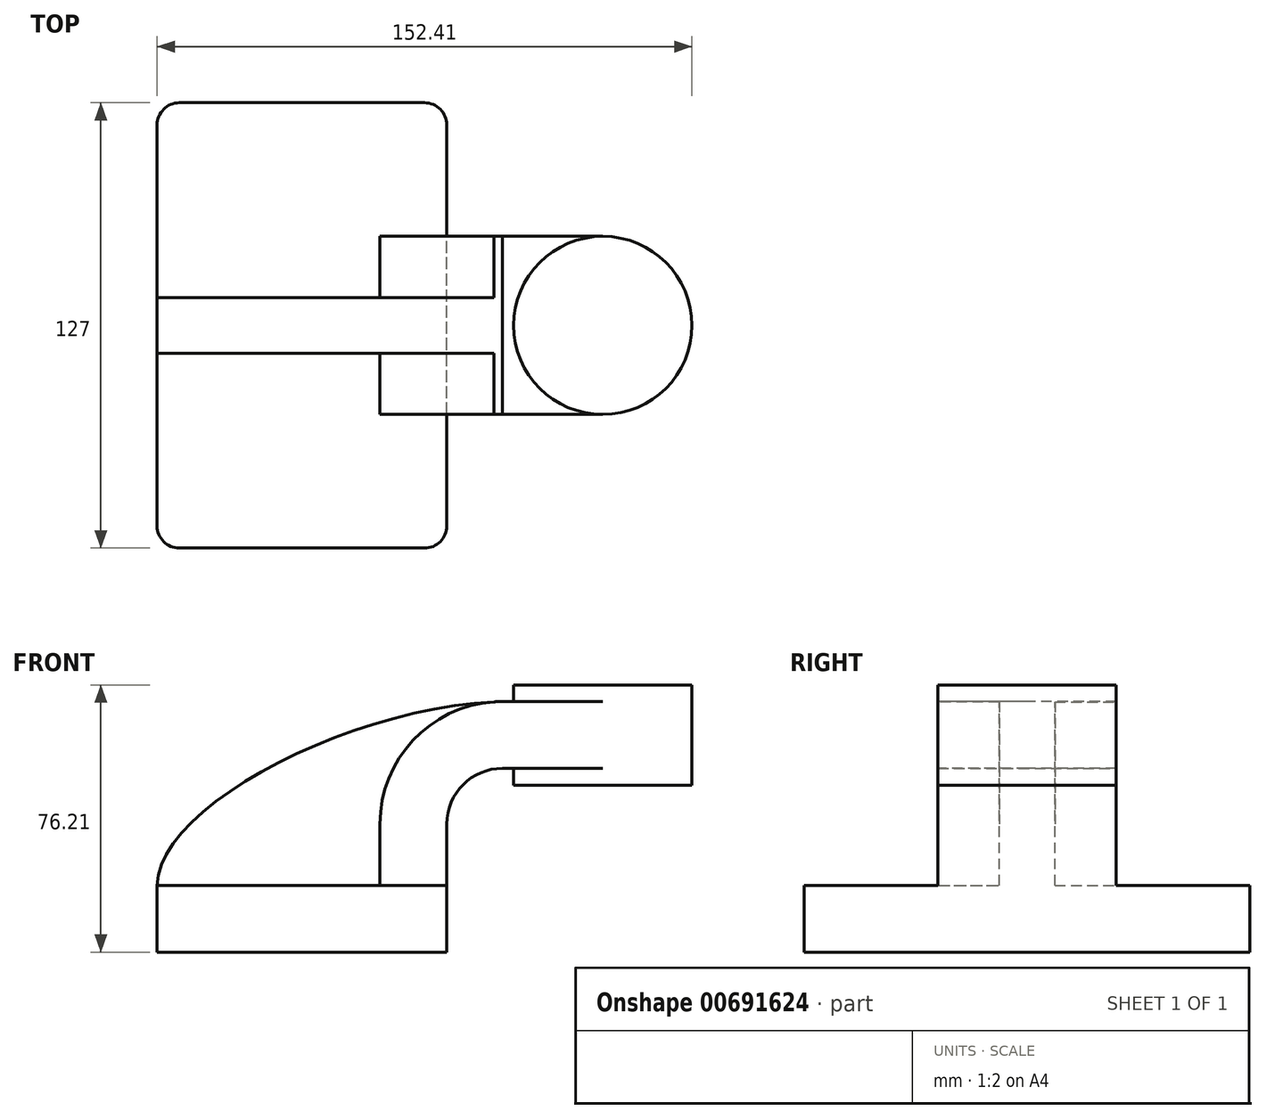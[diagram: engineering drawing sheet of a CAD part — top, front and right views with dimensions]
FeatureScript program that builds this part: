
annotation { "Feature Type Name" : "Feature", "Feature Type Description" : "" }
export const myFeature = defineFeature(function(context is Context, id is Id, definition is map)
    precondition{}
    {
        {
            var Q0;
            Q0=qCreatedBy(makeId("Front.planeOp"),FACE);
            var sketch = newSketch(context, id + "F0", { "sketchPlane" : qUnion([Q0])});
            skLineSegment(sketch, "E0.bottom", {"start": v(-41.28, 9.52) * mm, "end": v(41.27, 9.53) * mm});
            skLineSegment(sketch, "E0.top", {"start": v(-41.28, -9.52) * mm, "end": v(41.28, -9.52) * mm});
            skLineSegment(sketch, "E0.left", {"start": v(-41.28, 9.52) * mm, "end": v(-41.28, -9.53) * mm});
            skLineSegment(sketch, "E0.right", {"start": v(41.27, 9.53) * mm, "end": v(41.28, -9.52) * mm});
            skPoint(sketch, "E0.middle", {"position": v(0, 0) * mm});
            skLineSegment(sketch, "E1.bottom", {"start": v(111.12, 38.1) * mm, "end": v(60.32, 38.1) * mm});
            skLineSegment(sketch, "E1.top", {"start": v(111.12, 66.68) * mm, "end": v(60.32, 66.68) * mm});
            skLineSegment(sketch, "E1.left", {"start": v(111.12, 38.1) * mm, "end": v(111.12, 66.68) * mm});
            skLineSegment(sketch, "E1.right", {"start": v(60.32, 38.1) * mm, "end": v(60.32, 66.68) * mm});
            skPoint(sketch, "E1.middle", {"position": v(85.72, 52.39) * mm});
            skLineSegment(sketch, "E2", {"start": v(41.27, 9.53) * mm, "end": v(41.27, 27) * mm});
            skArc(sketch, "E3", {"start": v(41.27, 27) * mm, "mid": v(45.92, 38.23) * mm, "end": v(57.15, 42.88) * mm});
            skLineSegment(sketch, "E4", {"start": v(57.15, 42.88) * mm, "end": v(85.72, 42.88) * mm});
            skLineSegment(sketch, "E5.0", {"start": v(57.15, 61.93) * mm, "end": v(85.72, 61.93) * mm});
            skArc(sketch, "E5.1", {"start": v(22.22, 27) * mm, "mid": v(32.45, 51.7) * mm, "end": v(57.15, 61.93) * mm});
            skLineSegment(sketch, "E5.2", {"start": v(22.22, 9.53) * mm, "end": v(22.22, 27) * mm});
            skLineSegment(sketch, "E6", {"start": v(85.72, 38.1) * mm, "end": v(85.72, 66.68) * mm});
            skFitSpline(sketch, "E7", {"points": [v(-41.28, 9.53) * mm, v(57.15, 61.93) * mm], "startDerivative": vector(-0.04, 67.46) * mm, "endDerivative": vector(127.73, 2.9) * mm});
            skSolve(sketch);
        }
        {
            var Q0;
            Q0=makeQuery(id+"F0.imprint","IMPRINT",FACE,{"disambiguationData":[TD([[makeQuery(id+"F0.imprint","IMPRINT",EDGE,{"derivedFrom":sQuery(id+"F0.wireOp",EDGE,"E0.top")}),1.0]])]});
            extrude(context, id + "F1", {"entities" : qUnion([Q0]), "endBound" : BoundingType.SYMMETRIC, "depth" : 127 * mm, "offsetDistance" : 25.4 * mm});
        }
        {
            var Q0;
            {var subQ1=sQuery(id+"F0.wireOp",EDGE,"E2");Q0=makeQuery(id+"F0.imprint","IMPRINT",FACE,{"disambiguationData":[TD([[makeQuery(id+"F0.imprint","IMPRINT",EDGE,{"derivedFrom":subQ1}),1.0]])]});}
            var Q1;
            {var subQ0=sQuery(id+"F0.wireOp",EDGE,"E4");var subQ1=sQuery(id+"F0.wireOp",EDGE,"E1.right");var subQ2=makeQuery(id+"F0.imprint","INTERSECT",VERTEX,{"derivedFrom":[subQ1,subQ0]});Q1=makeQuery(id+"F0.imprint","IMPRINT",FACE,{"disambiguationData":[TD([[makeQuery(id+"F0.imprint","IMPRINT",EDGE,{"disambiguationData":[TD([[subQ2,-1.0]])],"derivedFrom":subQ1}),-1.0]])]});}
            extrude(context, id + "F2", {"entities" : qUnion([Q0, Q1]), "operationType" : NewBodyOperationType.ADD, "endBound" : BoundingType.SYMMETRIC, "depth" : 50.8 * mm, "offsetDistance" : 25.4 * mm});
        }
        {
            var Q0;
            {var subQ3=sQuery(id+"F0.wireOp",EDGE,"E5.2");Q0=makeQuery(id+"F0.imprint","IMPRINT",FACE,{"disambiguationData":[TD([[makeQuery(id+"F0.imprint","IMPRINT",EDGE,{"derivedFrom":subQ3}),1.0]])]});}
            extrude(context, id + "F3", {"entities" : qUnion([Q0]), "operationType" : NewBodyOperationType.ADD, "endBound" : BoundingType.SYMMETRIC, "depth" : 15.88 * mm, "offsetDistance" : 25.4 * mm});
        }
        {
            var Q0;
            {var subQ0=sQuery(id+"F0.wireOp",EDGE,"E1.left");Q0=makeQuery(id+"F0.imprint","IMPRINT",FACE,{"disambiguationData":[TD([[makeQuery(id+"F0.imprint","IMPRINT",EDGE,{"derivedFrom":subQ0}),1.0]])]});}
            var Q1;
            Q1=sQuery(id+"F0.wireOp",EDGE,"E6");
            revolve(context, id + "F4", {"operationType" : NewBodyOperationType.ADD, "entities" : qUnion([Q0]), "axis" : qUnion([Q1]), "revolveType" : RevolveType.FULL});
        }
        {
            var Q0;
            Q0=makeQuery(id+"F1.opExtrude","CAP_EDGE",EDGE,{"disambiguationData":[OSD([sQuery(id+"F0.wireOp",EDGE,"E0.right")])],"isStart":false});
            var Q1;
            Q1=makeQuery(id+"F1.opExtrude","CAP_EDGE",EDGE,{"disambiguationData":[OSD([sQuery(id+"F0.wireOp",EDGE,"E0.right")])],"isStart":true});
            var Q2;
            Q2=makeQuery(id+"F1.opExtrude","CAP_EDGE",EDGE,{"disambiguationData":[OSD([sQuery(id+"F0.wireOp",EDGE,"E0.left")])],"isStart":true});
            var Q3;
            Q3=makeQuery(id+"F1.opExtrude","CAP_EDGE",EDGE,{"disambiguationData":[OSD([sQuery(id+"F0.wireOp",EDGE,"E0.left")])],"isStart":false});
            fillet(context, id + "F5", {"entities" : qUnion([Q0, Q1, Q2, Q3]), "radius" : 6.35 * mm, "tangentPropagation" : true, "allowEdgeOverflow" : false});
        }
    });
